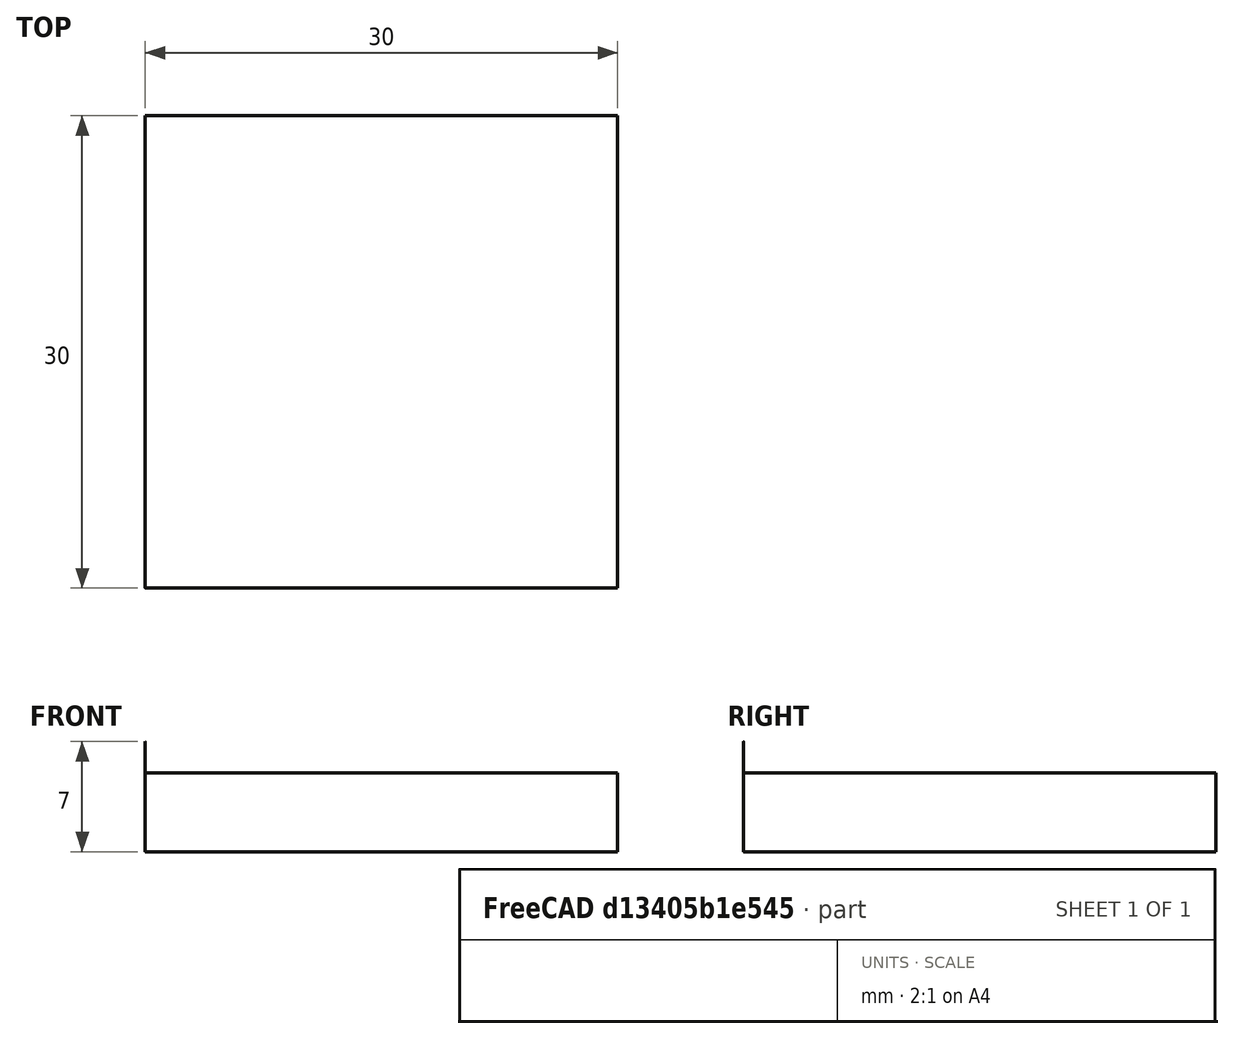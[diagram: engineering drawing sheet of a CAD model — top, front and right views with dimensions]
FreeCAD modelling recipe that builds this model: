
FCSTD DOCUMENT  (FreeCAD 1.0R39109 (Git))
Label: BoxWith20Grooves
License: All rights reserved
LicenseURL: https://en.wikipedia.org/wiki/All_rights_reserved
objects: Part::FeaturePython×3, App::DocumentObjectGroup×3, Path::FeaturePython×3, Part::Feature×1, App::FeaturePython×1
note: 5 computed .brp shape members not serialized (recipe doc carries the construction recipe); baked Part::Feature solids carry a one-line shape summary decoded from their .brp

FEATURE [Part::Feature] BoxWithPockets
  shape: bbox 30 x 30 x 5 mm, 106 faces (baked)
FEATURE [App::FeaturePython] SetupSheet  # Path/CAM operation (typed FeaturePython)
  ClearanceHeightExpression = OpStockZMax+SetupSheet.ClearanceHeightOffset
  ClearanceHeightOffset = 5
  CoolantMode = 0
  CoolantModes = None | Flood | Mist
  FinalDepthExpression = OpFinalDepth
  HorizRapid = 0
  SafeHeightExpression = OpStockZMax+SetupSheet.SafeHeightOffset
  SafeHeightOffset = 3
  StartDepthExpression = OpStartDepth
  StepDownExpression = OpToolDiameter
  VertRapid = 0
FEATURE [Part::FeaturePython] Clone  label="Model-BoxWithPockets"  # Draft clone (typed FeaturePython)
  AttacherType = Attacher::AttachEngine3D
  Fuse = false
  Objects = -> [BoxWithPockets]
  PathResource = Model
  Scale = (1,1,1)
FEATURE [App::DocumentObjectGroup] Model
  Group = -> [Clone]
FEATURE [Part::FeaturePython] ToolBit  label="Drill"  # Path/CAM toolbit (typed FeaturePython)
  BitPropertyNames = Chipload | Diameter | Flutes | Length | Material | TipAngle
  BitShape = <path>
  Chipload = 0
  Diameter = 0.005
  Flutes = 0
  Length = 7
  Material = 0
  ShapeName = drill
  TipAngle = 119
FEATURE [Path::FeaturePython] TC__Default_Tool  label="TC: Default Tool"  # Path/CAM operation (typed FeaturePython)
  HorizFeed = 0
  HorizRapid = 0
  SpindleDir = 0
  SpindleSpeed = 0
  Tool = -> ToolBit
  ToolNumber = 1
  VertFeed = 0
  VertRapid = 0
  expr: HorizRapid = SetupSheet.HorizRapid
  expr: VertRapid = SetupSheet.VertRapid
FEATURE [App::DocumentObjectGroup] Tools
  Group = -> [TC__Default_Tool]
FEATURE [Part::FeaturePython] Stock  # WARN: FeaturePython — macro-defined, semantics opaque (R4)
  Base = -> Model
  ExtXneg = 0.001
  ExtXpos = 0.001
  ExtYneg = 0.001
  ExtYpos = 0.001
  ExtZneg = 0.001
  ExtZpos = 0.001
  StockType = FromBase
FEATURE [Path::FeaturePython] Pocket_Shape  # Path/CAM operation (typed FeaturePython)
  Active = true
  AreaParams:
    Tolerance = 1e-07
    FitArcs = True
    Simplify = False
    CleanDistance = 0.0
    Accuracy = 0.01
    Unit = 1.0
    MinArcPoints = 4
    MaxArcPoints = 100
    ClipperScale = 10000000.0
    Fill = 0
    Coplanar = 0
    Reorient = True
    Outline = False
    Explode = False
    OpenMode = 0
    Deflection = 0.01
    SubjectFill = 0
    ClipFill = 0
    Offset = 0.0
    ExtraPass = 0
    Stepover = 0.0
    LastStepover = 0.0
    JoinType = 0
    EndType = 0
    MiterLimit = 2.0
    RoundPrecision = 0.0
    PocketMode = 1
    ToolRadius = 0.0025
    PocketExtraOffset = 0.0
    PocketStepover = 0.0025
    PocketLastStepover = 0.0
    FromCenter = True
    Angle = 0.0
    AngleShift = 0.0
    Shift = 0.0
    Thicken = False
    SectionCount = -1
    Stepdown = 1.0
    SectionOffset = 0.0
    SectionTolerance = 1e-06
    SectionMode = 2
    Project = False
  Base = -> [Clone]
  ClearanceHeight = 10.001
  CoolantMode = 0
  CutMode = 0
  CycleTime = Cycletime Error
  ExtensionCorners = true
  ExtensionLengthDefault = 0.0025
  ExtraOffset = 0
  FinalDepth = 4.999
  FinishDepth = 0
  KeepToolDown = false
  MinTravel = false
  OffsetPattern = 0
  OpFinalDepth = 4.999
  OpStartDepth = 5.001
  OpStockZMax = 5.001
  OpStockZMin = -0.001
  OpToolDiameter = 0.005
  PathParams = {'orientation': 1, 'feedrate': 0.0, 'feedrate_v': 0.0, 'verbose': True, 'resume_height': 8.001000000000001, 'retraction': 10.001000000000001, 'return_end': True, 'preamble': False, 'start': Vector (5.002500000000001, 27.142500099999996, 10.001000000000001)}
  PocketLastStepOver = 0
  SafeHeight = 8.001
  SplitArcs = false
  StartAt = 0
  StartDepth = 5.001
  StartPoint = (0,0,0)
  StepDown = 0.005
  StepOver = 50
  ToolController = -> TC__Default_Tool
  UseOutline = false
  UseRestMachining = false
  UseStartPoint = false
  ZigZagAngle = 0
  expr: ClearanceHeight = OpStockZMax + SetupSheet.ClearanceHeightOffset
  expr: ExtensionLengthDefault = OpToolDiameter / 2
  expr: FinalDepth = OpFinalDepth
  expr: SafeHeight = OpStockZMax + SetupSheet.SafeHeightOffset
  expr: StartDepth = OpStartDepth
  expr: StepDown = OpToolDiameter
FEATURE [App::DocumentObjectGroup] Operations
  Group = -> [Pocket_Shape]
FEATURE [Path::FeaturePython] Job  # Path/CAM operation (typed FeaturePython)
  CycleTime = 00:00:00
  Fixtures = G54
  GeometryTolerance = 0.01
  JobType = 0
  Model = -> Model
  Operations = -> Operations
  OrderOutputBy = 0
  PostProcessor = 14
  SetupSheet = -> SetupSheet
  SplitOutput = false
  Stock = -> Stock
  Tools = -> Tools
note: 1 file-system path scrubbed to <path> (originals preserved in the JSON sidecar)
